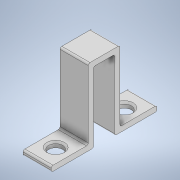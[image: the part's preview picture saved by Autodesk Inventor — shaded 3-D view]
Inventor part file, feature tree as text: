
AUTODESK INVENTOR PART (.ipt)
format: ipt  version: 2020 (Build 240168000, 168)  size: 142,336 bytes
history: native  units: in
note: dims shown in document units (in); Inventor stores cm internally (conversion verified against a paired STEP export)
features: sketch x2, extrude x1, hole x1, fillet x1
ambient origin geometry x8: Origin, YZ Plane, XZ Plane, XY Plane, X Axis, Y Axis, Z Axis, Center Point
bodies: Solid1 (feature_tree)
feature tree (5):
  extrude  "Extrusion1"  Depth=0.4724in
  hole  "Hole1"  [1 undecoded]
  fillet  "Fillet1"  Radius=0.0591in
  sketch  "Sketch1"  dims[d0=0.4724in d1=0.4724in]
  sketch  "Sketch2"  dims[d2=0.2362in d3=0.7874in d4=0.0591in d5=0.315in d6=0.0in d7=0.1575in d8=0.7874in d9=0.1969in d10=0.0787in d11=90.0deg d12=0.315in d13=0.8108in d14=0.0197in]
note: 1 required parameter value undecoded (feature->parameter linkage not recoverable at this tier; creation-order binding heuristic only, values carry confidence <= 0.55)
